# Revit family: NBS_DudleyIndustriesLimited_PprTwlDpnsrs_SmallPlatinumRange_77015CB
name_source: partatom
category: Specialty Equipment
units: mm (PartAtom-declared; Revit-internal decimal feet)

## family parameters
Cut with Voids When Loaded = No
Host = Face
Part Type = Normal
Room Calculation Point = No
Round Connector Dimension = Use Diameter
Shared = No

## types (1)
- 77015CB
    AssetType = Fixed
    BIMObjectName = NBS_DudleyIndustriesLimited_PaperTowelDispensers_SmallPlatinumRange_77015CB
    Category = Pr_40_70_22_62:Paper towel dispensers
    Color = Brushed with clear lacquer
    Default Elevation = 1300 mm  [stored 4.26509 ft]
    Description = Elegant small stainless steel paper towel dispenser
    DispenserCaseMaterial = NBS_DudleyIndustries_StainlessSteel_Polished
    DispenserHeigth = 317 mm  [stored 1.04003 ft]
    DispenserLockMaterial = NBS_DudleyIndustries_StainlessSteel_Polished
    DispenserWidth = 290 mm  [stored 0.951444 ft]
    Finish = Brushed with Clear Lacquer
    HasProtectiveEarth = No
    IfcExportAs = IfcFurnitureType
    IfcExportType = NOTDEFINED
    IsBuiltIn = No
    ManufacturerName = Dudley Industries Limited
    ManufacturerURL = www.dudleyindustries.com
    Material = Stainless steel
    ModelNumber = 77015CB
    ModelReference = Small Platinum Range 77015CB
    NBSCertification = www.nationalbimlibrary.com/cert/0onmyyz4
    NBSDescription = Paper towel dispensers
    NBSReference = 45-35-72/344
    Name = PaperTowelDispensers_SmallPlatinumRange_77015CB_DudleyIndustriesLimited_NBS
    NominalDepth = 145 mm  [stored 0.475722 ft]
    NominalHeight = 317 mm  [stored 1.04003 ft]
    NominalLength = 290 mm  [stored 0.951444 ft]
    NominalWidth = 290 mm  [stored 0.951444 ft]
    NumberOfPoles = 0
    PowerFactor = 0
    ProductInformation = https://www.dudleyindustries.com
    Size = 317mm x 290mm x 145mm
    Status = UNSET
    Uniclass2015Code = Pr_40_70_22_62
    Uniclass2015Title = Paper towel dispensers
    Uniclass2015Version = Products v1.22
    Version = 1
    WarrantyDurationUnit = year

note: [stored X ft] marks values corroborated as IEEE doubles in the binary element streams (Revit-internal decimal feet)

## geometry (parser evidence)
native form markers: Sweep x2
no freeform markers — native parametric forms only
